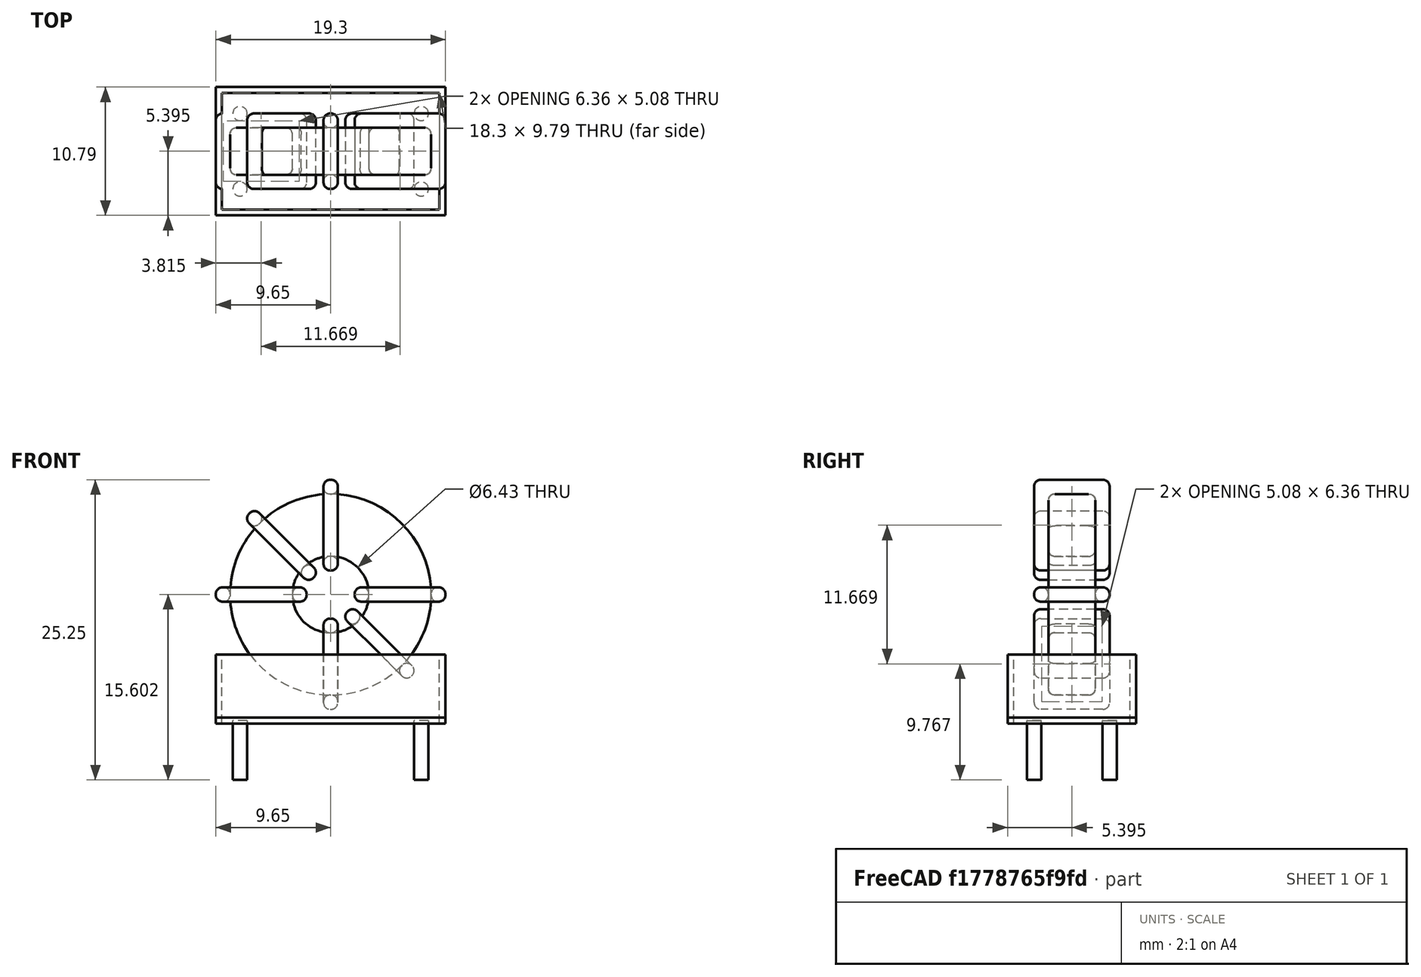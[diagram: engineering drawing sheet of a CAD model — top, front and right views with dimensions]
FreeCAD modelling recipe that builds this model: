
FCSTD DOCUMENT  (FreeCAD 0.16R6703 (Git))
Label: L_CommonModeChoke_Toroid_Vertical_L19.3mm_W10.8mm_Px6.35mm_Py15.24mm_Bourns_8100series
License: All rights reserved
LicenseURL: http://en.wikipedia.org/wiki/All_rights_reserved
objects: Sketcher::SketchObject×8, PartDesign::Pad×8, PartDesign::Fillet×5, Spreadsheet::Sheet×1
note: 29 computed .brp shape members not serialized (recipe doc carries the construction recipe); baked Part::Feature solids carry a one-line shape summary decoded from their .brp

FEATURE [Spreadsheet::Sheet] Spreadsheet  label="dimensions"
  cells = A1=Wx; B1(Wx)=19.304; C1(WW)=6.434666666666666; D1(iWx)=19.304; A2=Wy; B2(Wy)=6.35; D2(iWy)=10.795; A3=RM; B3(RMx)=6.35; C3(RMy)=15.24; A4=d_wire; B4(d_wire)=1.2; A5=H; B5(H)=31; A6=offsetx; B6(offsetx)=2.032
FEATURE [Sketcher::SketchObject] Sketch
  Placement = pos=(7.62,-3.175,0) rot=(1,0,0;1.5708rad)
  expr: Placement.Base.x = Spreadsheet.RMy / 2
  expr: Constraints[4] = Spreadsheet.WW / 2
  expr: Placement.Base.y = -Spreadsheet.RMx / 2
  expr: Constraints[0] = Spreadsheet.Wx / 2 - Spreadsheet.d_wire
  expr: Constraints[2] = Spreadsheet.Wx / 2 + Spreadsheet.d_wire + 0.5
  sketch-geometry (2):
    g0: Circle CenterX=0 CenterY=11.352 CenterZ=0 NormalX=0 NormalY=0 NormalZ=1 Radius=8.452
    g1: Circle CenterX=0 CenterY=11.352 CenterZ=0 NormalX=0 NormalY=0 NormalZ=1 Radius=3.21733
  constraints (5):
    c: Radius(g0) = 8.452
    c: DistanceX(g-1,g0) = 0
    c: DistanceY(g-1,g0) = 11.352
    c: Coincident(g1,g0)
    c: Radius(g1) = 3.21733
FEATURE [PartDesign::Pad] Pad
  Length = 3.95
  Length2 = 100
  Midplane = true
  Placement = pos=(7.62,-3.175,0) rot=(1,0,0;1.5708rad)
  Sketch = -> Sketch
  Type = 0
  expr: Length = Spreadsheet.Wy - 2 * Spreadsheet.d_wire
FEATURE [Sketcher::SketchObject] Sketch001
  Placement = pos=(0,0,0.75) rot=(0,0,1;0rad)
  expr: Constraints[4] = Spreadsheet.RMy
  expr: Constraints[2] = -Spreadsheet.RMx
  expr: Constraints[1] = Spreadsheet.d_wire / 2
  sketch-geometry (4):
    g0: Circle CenterX=0 CenterY=0 CenterZ=0 NormalX=0 NormalY=0 NormalZ=1 Radius=0.6
    g1: Circle CenterX=15.24 CenterY=-6.35 CenterZ=0 NormalX=0 NormalY=0 NormalZ=1 Radius=0.6
    g2: Circle CenterX=0 CenterY=-6.35 CenterZ=0 NormalX=0 NormalY=0 NormalZ=1 Radius=0.6
    g3: Circle CenterX=15.24 CenterY=0 CenterZ=0 NormalX=0 NormalY=0 NormalZ=1 Radius=0.6
  constraints (11):
    c: Equal(g0,g1)
    c: Radius(g0) = 0.6
    c: DistanceY(g-1,g1) = -6.35
    c: Coincident(g0,g-1)
    c: DistanceX(g-1,g1) = 15.24
    c: PointOnObject(g2,g-2)
    c: DistanceY(g-1,g3) = 0
    c: DistanceY(g2,g1) = 0
    c: DistanceX(g3,g1) = 0
    c: Equal(g3,g2)
    c: Equal(g2,g1)
FEATURE [PartDesign::Pad] Pad001
  Length = 5
  Length2 = 0
  Placement = pos=(0,0,0.75) rot=(0,0,1;0rad)
  Reversed = true
  Sketch = -> Sketch001
  Type = 0
FEATURE [PartDesign::Fillet] Fillet
  Base = -> Pad [Edge6,Edge3,Edge2]
  Placement = pos=(7.62,-3.175,0) rot=(1,0,0;1.5708rad)
  Radius = 0.5
FEATURE [Sketcher::SketchObject] Sketch003
  Placement = pos=(7.62,0,11.352) rot=(1,0,0;3.14159rad)
  expr: Placement.Base.x = Spreadsheet.RMy / 2
  expr: Constraints[18] = Spreadsheet.d_wire
  expr: Constraints[16] = Spreadsheet.d_wire
  expr: Constraints[19] = Spreadsheet.d_wire
  expr: Constraints[17] = Spreadsheet.d_wire
  expr: Placement.Base.y = -1 * (Spreadsheet.RMx - Spreadsheet.Wy) / 2
  expr: Constraints[21] = (Spreadsheet.Wx - Spreadsheet.WW) / 2 - Spreadsheet.d_wire
  expr: Constraints[22] = Spreadsheet.Wx / 2 - Spreadsheet.d_wire
  expr: Constraints[43] = Spreadsheet.d_wire
  expr: Constraints[48] = Spreadsheet.Wx - Spreadsheet.d_wire * 2
  expr: Constraints[49] = Spreadsheet.Wy
  expr: Placement.Base.z = Spreadsheet.Wx / 2 + Spreadsheet.d_wire + 0.5
  sketch-geometry (16):
    g0: LineSegment StartX=-2.01733 StartY=0 StartZ=0 EndX=-9.652 EndY=0 EndZ=0
    g1: LineSegment StartX=-9.652 StartY=0 StartZ=0 EndX=-9.652 EndY=6.35 EndZ=0
    g2: LineSegment StartX=-9.652 StartY=6.35 StartZ=0 EndX=-2.01733 EndY=6.35 EndZ=0
    g3: LineSegment StartX=-2.01733 StartY=6.35 StartZ=0 EndX=-2.01733 EndY=0 EndZ=0
    g4: LineSegment StartX=-8.452 StartY=5.15 StartZ=0 EndX=-3.21733 EndY=5.15 EndZ=0
    g5: LineSegment StartX=-3.21733 StartY=5.15 StartZ=0 EndX=-3.21733 EndY=1.2 EndZ=0
    g6: LineSegment StartX=-3.21733 StartY=1.2 StartZ=0 EndX=-8.452 EndY=1.2 EndZ=0
    g7: LineSegment StartX=-8.452 StartY=1.2 StartZ=0 EndX=-8.452 EndY=5.15 EndZ=0
    g8: LineSegment StartX=2.01733 StartY=6.35 StartZ=0 EndX=9.652 EndY=6.35 EndZ=0
    g9: LineSegment StartX=9.652 StartY=6.35 StartZ=0 EndX=9.652 EndY=0 EndZ=0
    g10: LineSegment StartX=9.652 StartY=0 StartZ=0 EndX=2.01733 EndY=0 EndZ=0
    g11: LineSegment StartX=2.01733 StartY=0 StartZ=0 EndX=2.01733 EndY=6.35 EndZ=0
    g12: LineSegment StartX=3.21733 StartY=5.15 StartZ=0 EndX=8.452 EndY=5.15 EndZ=0
    g13: LineSegment StartX=8.452 StartY=5.15 StartZ=0 EndX=8.452 EndY=1.2 EndZ=0
    g14: LineSegment StartX=8.452 StartY=1.2 StartZ=0 EndX=3.21733 EndY=1.2 EndZ=0
    g15: LineSegment StartX=3.21733 StartY=1.2 StartZ=0 EndX=3.21733 EndY=5.15 EndZ=0
  constraints (50):
    c: Horizontal(g0)
    c: Coincident(g1,g0)
    c: Vertical(g1)
    c: Coincident(g2,g1)
    c: Horizontal(g2)
    c: Coincident(g3,g2)
    c: Coincident(g3,g0)
    c: Vertical(g3)
    c: Coincident(g4,g5)
    c: Coincident(g5,g6)
    c: Coincident(g6,g7)
    c: Coincident(g7,g4)
    c: Horizontal(g4)
    c: Horizontal(g6)
    c: Vertical(g5)
    c: Vertical(g7)
    c: DistanceX(g1,g4) = 1.2
    c: DistanceY(g4,g1) = 1.2
    c: DistanceX(g5,g0) = 1.2
    c: DistanceY(g0,g5) = 1.2
    c: DistanceY(g-1,g0) = 0
    c: DistanceX(g6,g6) = 5.23467
    c: DistanceX(g6,g-1) = 8.452
    c: Coincident(g8,g9)
    c: Coincident(g9,g10)
    c: Coincident(g10,g11)
    c: Coincident(g11,g8)
    c: Horizontal(g8)
    c: Horizontal(g10)
    c: Vertical(g9)
    c: Vertical(g11)
    c: Coincident(g12,g13)
    c: Coincident(g13,g14)
    c: Coincident(g14,g15)
    c: Coincident(g15,g12)
    c: Horizontal(g12)
    c: Horizontal(g14)
    c: Vertical(g13)
    c: Vertical(g15)
    c: DistanceY(g8,g2) = 0
    c: DistanceY(g10,g0) = 0
    c: DistanceY(g14,g5) = 0
    c: DistanceY(g12,g4) = 0
    c: DistanceX(g8,g12) = 1.2
    c: Equal(g8,g2)
    c: Equal(g12,g4)
    c: Equal(g9,g1)
    c: Equal(g13,g7)
    c: DistanceX(g4,g12) = 16.904
    c: DistanceY(g0,g1) = 6.35
FEATURE [PartDesign::Pad] Pad002
  Length = 1.2
  Length2 = 100
  Midplane = true
  Placement = pos=(7.62,0,11.352) rot=(1,0,0;3.14159rad)
  Sketch = -> Sketch003
  Type = 0
  expr: Length = Spreadsheet.d_wire
FEATURE [PartDesign::Fillet] Fillet001
  Base = -> Pad002 [Edge38,Edge41,Edge42,Edge43,Edge29,Edge32,Edge33,Edge34,Edge25,Edge35,Edge36,Edge13,Edge14,Edge15,Edge16,Edge17,Edge18,Edge19,Edge1,Edge2,Edge3,Edge4,Edge5,Edge6,Edge7,Edge37,Edge39,Edge40,Edge20,Edge23,Edge24,Edge21,Edge22,Edge8,Edge9,Edge10,Edge11,Edge12,Edge26,Edge27,+8 more]
  Placement = pos=(7.62,0,11.352) rot=(1,0,0;3.14159rad)
  Radius = 0.564
  expr: Radius = Spreadsheet.d_wire * 0.47
FEATURE [Sketcher::SketchObject] Sketch004
  Placement = pos=(7.62,0,11.352) rot=(0.92388,0,0.382683;3.14159rad)
  expr: Placement.Base.x = Spreadsheet.RMy / 2
  expr: Constraints[18] = Spreadsheet.d_wire
  expr: Constraints[16] = Spreadsheet.d_wire
  expr: Constraints[19] = Spreadsheet.d_wire
  expr: Constraints[17] = Spreadsheet.d_wire
  expr: Placement.Base.y = -1 * (Spreadsheet.RMx - Spreadsheet.Wy) / 2
  expr: Constraints[21] = (Spreadsheet.Wx - Spreadsheet.WW) / 2 - Spreadsheet.d_wire
  expr: Constraints[22] = Spreadsheet.Wx / 2 - Spreadsheet.d_wire
  expr: Constraints[43] = Spreadsheet.d_wire
  expr: Constraints[48] = Spreadsheet.Wx - 2 * Spreadsheet.d_wire
  expr: Constraints[49] = Spreadsheet.Wy
  expr: Placement.Base.z = Spreadsheet.Wx / 2 + Spreadsheet.d_wire + 0.5
  sketch-geometry (16):
    g0: LineSegment StartX=-2.01733 StartY=0 StartZ=0 EndX=-9.652 EndY=0 EndZ=0
    g1: LineSegment StartX=-9.652 StartY=0 StartZ=0 EndX=-9.652 EndY=6.35 EndZ=0
    g2: LineSegment StartX=-9.652 StartY=6.35 StartZ=0 EndX=-2.01733 EndY=6.35 EndZ=0
    g3: LineSegment StartX=-2.01733 StartY=6.35 StartZ=0 EndX=-2.01733 EndY=0 EndZ=0
    g4: LineSegment StartX=-8.452 StartY=5.15 StartZ=0 EndX=-3.21733 EndY=5.15 EndZ=0
    g5: LineSegment StartX=-3.21733 StartY=5.15 StartZ=0 EndX=-3.21733 EndY=1.2 EndZ=0
    g6: LineSegment StartX=-3.21733 StartY=1.2 StartZ=0 EndX=-8.452 EndY=1.2 EndZ=0
    g7: LineSegment StartX=-8.452 StartY=1.2 StartZ=0 EndX=-8.452 EndY=5.15 EndZ=0
    g8: LineSegment StartX=2.01733 StartY=6.35 StartZ=0 EndX=9.652 EndY=6.35 EndZ=0
    g9: LineSegment StartX=9.652 StartY=6.35 StartZ=0 EndX=9.652 EndY=0 EndZ=0
    g10: LineSegment StartX=9.652 StartY=0 StartZ=0 EndX=2.01733 EndY=0 EndZ=0
    g11: LineSegment StartX=2.01733 StartY=0 StartZ=0 EndX=2.01733 EndY=6.35 EndZ=0
    g12: LineSegment StartX=3.21733 StartY=5.15 StartZ=0 EndX=8.452 EndY=5.15 EndZ=0
    g13: LineSegment StartX=8.452 StartY=5.15 StartZ=0 EndX=8.452 EndY=1.2 EndZ=0
    g14: LineSegment StartX=8.452 StartY=1.2 StartZ=0 EndX=3.21733 EndY=1.2 EndZ=0
    g15: LineSegment StartX=3.21733 StartY=1.2 StartZ=0 EndX=3.21733 EndY=5.15 EndZ=0
  constraints (50):
    c: Horizontal(g0)
    c: Coincident(g1,g0)
    c: Vertical(g1)
    c: Coincident(g2,g1)
    c: Horizontal(g2)
    c: Coincident(g3,g2)
    c: Coincident(g3,g0)
    c: Vertical(g3)
    c: Coincident(g4,g5)
    c: Coincident(g5,g6)
    c: Coincident(g6,g7)
    c: Coincident(g7,g4)
    c: Horizontal(g4)
    c: Horizontal(g6)
    c: Vertical(g5)
    c: Vertical(g7)
    c: DistanceX(g1,g4) = 1.2
    c: DistanceY(g4,g1) = 1.2
    c: DistanceX(g5,g0) = 1.2
    c: DistanceY(g0,g5) = 1.2
    c: DistanceY(g-1,g0) = 0
    c: DistanceX(g6,g6) = 5.23467
    c: DistanceX(g6,g-1) = 8.452
    c: Coincident(g8,g9)
    c: Coincident(g9,g10)
    c: Coincident(g10,g11)
    c: Coincident(g11,g8)
    c: Horizontal(g8)
    c: Horizontal(g10)
    c: Vertical(g9)
    c: Vertical(g11)
    c: Coincident(g12,g13)
    c: Coincident(g13,g14)
    c: Coincident(g14,g15)
    c: Coincident(g15,g12)
    c: Horizontal(g12)
    c: Horizontal(g14)
    c: Vertical(g13)
    c: Vertical(g15)
    c: DistanceY(g8,g2) = 0
    c: DistanceY(g10,g0) = 0
    c: DistanceY(g14,g5) = 0
    c: DistanceY(g12,g4) = 0
    c: DistanceX(g8,g12) = 1.2
    c: Equal(g8,g2)
    c: Equal(g12,g4)
    c: Equal(g9,g1)
    c: Equal(g13,g7)
    c: DistanceX(g4,g12) = 16.904
    c: DistanceY(g0,g1) = 6.35
FEATURE [PartDesign::Pad] Pad003
  Length = 1.2
  Length2 = 100
  Midplane = true
  Placement = pos=(7.62,0,11.352) rot=(0.92388,0,0.382683;3.14159rad)
  Sketch = -> Sketch004
  Type = 0
  expr: Length = Spreadsheet.d_wire
FEATURE [PartDesign::Fillet] Fillet002
  Base = -> Pad003 [Edge38,Edge41,Edge42,Edge43,Edge29,Edge32,Edge33,Edge34,Edge25,Edge35,Edge36,Edge13,Edge14,Edge15,Edge16,Edge17,Edge18,Edge19,Edge1,Edge2,Edge3,Edge4,Edge5,Edge6,Edge7,Edge37,Edge39,Edge40,Edge20,Edge23,Edge24,Edge21,Edge22,Edge8,Edge9,Edge10,Edge11,Edge12,Edge26,Edge27,+8 more]
  Placement = pos=(7.62,0,11.352) rot=(0.92388,0,0.382683;3.14159rad)
  Radius = 0.564
  expr: Radius = Spreadsheet.d_wire * 0.47
FEATURE [Sketcher::SketchObject] Sketch005
  Placement = pos=(7.62,0,11.352) rot=(0.92388,0,-0.382683;3.14159rad)
  expr: Placement.Base.x = Spreadsheet.RMy / 2
  expr: Constraints[18] = Spreadsheet.d_wire
  expr: Constraints[16] = Spreadsheet.d_wire
  expr: Constraints[19] = Spreadsheet.d_wire
  expr: Constraints[17] = Spreadsheet.d_wire
  expr: Placement.Base.y = -1 * (Spreadsheet.RMx - Spreadsheet.Wy) / 2
  expr: Constraints[21] = (Spreadsheet.Wx - Spreadsheet.WW) / 2 - Spreadsheet.d_wire
  expr: Constraints[22] = Spreadsheet.Wx / 2 - Spreadsheet.d_wire
  expr: Constraints[43] = Spreadsheet.d_wire
  expr: Constraints[48] = Spreadsheet.Wx - 2 * Spreadsheet.d_wire
  expr: Constraints[49] = Spreadsheet.Wy
  expr: Placement.Base.z = Spreadsheet.Wx / 2 + Spreadsheet.d_wire + 0.5
  sketch-geometry (16):
    g0: LineSegment StartX=-2.01733 StartY=0 StartZ=0 EndX=-9.652 EndY=0 EndZ=0
    g1: LineSegment StartX=-9.652 StartY=0 StartZ=0 EndX=-9.652 EndY=6.35 EndZ=0
    g2: LineSegment StartX=-9.652 StartY=6.35 StartZ=0 EndX=-2.01733 EndY=6.35 EndZ=0
    g3: LineSegment StartX=-2.01733 StartY=6.35 StartZ=0 EndX=-2.01733 EndY=0 EndZ=0
    g4: LineSegment StartX=-8.452 StartY=5.15 StartZ=0 EndX=-3.21733 EndY=5.15 EndZ=0
    g5: LineSegment StartX=-3.21733 StartY=5.15 StartZ=0 EndX=-3.21733 EndY=1.2 EndZ=0
    g6: LineSegment StartX=-3.21733 StartY=1.2 StartZ=0 EndX=-8.452 EndY=1.2 EndZ=0
    g7: LineSegment StartX=-8.452 StartY=1.2 StartZ=0 EndX=-8.452 EndY=5.15 EndZ=0
    g8: LineSegment StartX=2.01733 StartY=6.35 StartZ=0 EndX=9.652 EndY=6.35 EndZ=0
    g9: LineSegment StartX=9.652 StartY=6.35 StartZ=0 EndX=9.652 EndY=0 EndZ=0
    g10: LineSegment StartX=9.652 StartY=0 StartZ=0 EndX=2.01733 EndY=0 EndZ=0
    g11: LineSegment StartX=2.01733 StartY=0 StartZ=0 EndX=2.01733 EndY=6.35 EndZ=0
    g12: LineSegment StartX=3.21733 StartY=5.15 StartZ=0 EndX=8.452 EndY=5.15 EndZ=0
    g13: LineSegment StartX=8.452 StartY=5.15 StartZ=0 EndX=8.452 EndY=1.2 EndZ=0
    g14: LineSegment StartX=8.452 StartY=1.2 StartZ=0 EndX=3.21733 EndY=1.2 EndZ=0
    g15: LineSegment StartX=3.21733 StartY=1.2 StartZ=0 EndX=3.21733 EndY=5.15 EndZ=0
  constraints (50):
    c: Horizontal(g0)
    c: Coincident(g1,g0)
    c: Vertical(g1)
    c: Coincident(g2,g1)
    c: Horizontal(g2)
    c: Coincident(g3,g2)
    c: Coincident(g3,g0)
    c: Vertical(g3)
    c: Coincident(g4,g5)
    c: Coincident(g5,g6)
    c: Coincident(g6,g7)
    c: Coincident(g7,g4)
    c: Horizontal(g4)
    c: Horizontal(g6)
    c: Vertical(g5)
    c: Vertical(g7)
    c: DistanceX(g1,g4) = 1.2
    c: DistanceY(g4,g1) = 1.2
    c: DistanceX(g5,g0) = 1.2
    c: DistanceY(g0,g5) = 1.2
    c: DistanceY(g-1,g0) = 0
    c: DistanceX(g6,g6) = 5.23467
    c: DistanceX(g6,g-1) = 8.452
    c: Coincident(g8,g9)
    c: Coincident(g9,g10)
    c: Coincident(g10,g11)
    c: Coincident(g11,g8)
    c: Horizontal(g8)
    c: Horizontal(g10)
    c: Vertical(g9)
    c: Vertical(g11)
    c: Coincident(g12,g13)
    c: Coincident(g13,g14)
    c: Coincident(g14,g15)
    c: Coincident(g15,g12)
    c: Horizontal(g12)
    c: Horizontal(g14)
    c: Vertical(g13)
    c: Vertical(g15)
    c: DistanceY(g8,g2) = 0
    c: DistanceY(g10,g0) = 0
    c: DistanceY(g14,g5) = 0
    c: DistanceY(g12,g4) = 0
    c: DistanceX(g8,g12) = 1.2
    c: Equal(g8,g2)
    c: Equal(g12,g4)
    c: Equal(g9,g1)
    c: Equal(g13,g7)
    c: DistanceX(g4,g12) = 16.904
    c: DistanceY(g0,g1) = 6.35
FEATURE [PartDesign::Pad] Pad004
  Length = 1.2
  Length2 = 100
  Midplane = true
  Placement = pos=(7.62,0,11.352) rot=(0.92388,0,-0.382683;3.14159rad)
  Sketch = -> Sketch005
  Type = 0
  expr: Length = Spreadsheet.d_wire
FEATURE [PartDesign::Fillet] Fillet003
  Base = -> Pad004 [Edge38,Edge41,Edge42,Edge43,Edge29,Edge32,Edge33,Edge34,Edge25,Edge35,Edge36,Edge13,Edge14,Edge15,Edge16,Edge17,Edge18,Edge19,Edge1,Edge2,Edge3,Edge4,Edge5,Edge6,Edge7,Edge37,Edge39,Edge40,Edge20,Edge23,Edge24,Edge21,Edge22,Edge8,Edge9,Edge10,Edge11,Edge12,Edge26,Edge27,+8 more]
  Placement = pos=(7.62,0,11.352) rot=(0.92388,0,-0.382683;3.14159rad)
  Radius = 0.564
  expr: Radius = Spreadsheet.d_wire * 0.47
FEATURE [Sketcher::SketchObject] Sketch006
  Placement = pos=(7.62,0,11.352) rot=(0.707107,0,0.707107;3.14159rad)
  expr: Placement.Base.x = Spreadsheet.RMy / 2
  expr: Constraints[18] = Spreadsheet.d_wire
  expr: Constraints[16] = Spreadsheet.d_wire
  expr: Constraints[19] = Spreadsheet.d_wire
  expr: Constraints[17] = Spreadsheet.d_wire
  expr: Placement.Base.y = -1 * (Spreadsheet.RMx - Spreadsheet.Wy) / 2
  expr: Constraints[21] = (Spreadsheet.Wx - Spreadsheet.WW) / 2 - Spreadsheet.d_wire
  expr: Constraints[22] = Spreadsheet.Wx / 2 - Spreadsheet.d_wire
  expr: Constraints[43] = Spreadsheet.d_wire
  expr: Constraints[48] = Spreadsheet.Wx - Spreadsheet.d_wire * 2
  expr: Constraints[49] = Spreadsheet.Wy
  expr: Placement.Base.z = Spreadsheet.Wx / 2 + Spreadsheet.d_wire + 0.5
  sketch-geometry (16):
    g0: LineSegment StartX=-2.01733 StartY=0 StartZ=0 EndX=-9.652 EndY=0 EndZ=0
    g1: LineSegment StartX=-9.652 StartY=0 StartZ=0 EndX=-9.652 EndY=6.35 EndZ=0
    g2: LineSegment StartX=-9.652 StartY=6.35 StartZ=0 EndX=-2.01733 EndY=6.35 EndZ=0
    g3: LineSegment StartX=-2.01733 StartY=6.35 StartZ=0 EndX=-2.01733 EndY=0 EndZ=0
    g4: LineSegment StartX=-8.452 StartY=5.15 StartZ=0 EndX=-3.21733 EndY=5.15 EndZ=0
    g5: LineSegment StartX=-3.21733 StartY=5.15 StartZ=0 EndX=-3.21733 EndY=1.2 EndZ=0
    g6: LineSegment StartX=-3.21733 StartY=1.2 StartZ=0 EndX=-8.452 EndY=1.2 EndZ=0
    g7: LineSegment StartX=-8.452 StartY=1.2 StartZ=0 EndX=-8.452 EndY=5.15 EndZ=0
    g8: LineSegment StartX=2.01733 StartY=6.35 StartZ=0 EndX=9.652 EndY=6.35 EndZ=0
    g9: LineSegment StartX=9.652 StartY=6.35 StartZ=0 EndX=9.652 EndY=0 EndZ=0
    g10: LineSegment StartX=9.652 StartY=0 StartZ=0 EndX=2.01733 EndY=0 EndZ=0
    g11: LineSegment StartX=2.01733 StartY=0 StartZ=0 EndX=2.01733 EndY=6.35 EndZ=0
    g12: LineSegment StartX=3.21733 StartY=5.15 StartZ=0 EndX=8.452 EndY=5.15 EndZ=0
    g13: LineSegment StartX=8.452 StartY=5.15 StartZ=0 EndX=8.452 EndY=1.2 EndZ=0
    g14: LineSegment StartX=8.452 StartY=1.2 StartZ=0 EndX=3.21733 EndY=1.2 EndZ=0
    g15: LineSegment StartX=3.21733 StartY=1.2 StartZ=0 EndX=3.21733 EndY=5.15 EndZ=0
  constraints (50):
    c: Horizontal(g0)
    c: Coincident(g1,g0)
    c: Vertical(g1)
    c: Coincident(g2,g1)
    c: Horizontal(g2)
    c: Coincident(g3,g2)
    c: Coincident(g3,g0)
    c: Vertical(g3)
    c: Coincident(g4,g5)
    c: Coincident(g5,g6)
    c: Coincident(g6,g7)
    c: Coincident(g7,g4)
    c: Horizontal(g4)
    c: Horizontal(g6)
    c: Vertical(g5)
    c: Vertical(g7)
    c: DistanceX(g1,g4) = 1.2
    c: DistanceY(g4,g1) = 1.2
    c: DistanceX(g5,g0) = 1.2
    c: DistanceY(g0,g5) = 1.2
    c: DistanceY(g-1,g0) = 0
    c: DistanceX(g6,g6) = 5.23467
    c: DistanceX(g6,g-1) = 8.452
    c: Coincident(g8,g9)
    c: Coincident(g9,g10)
    c: Coincident(g10,g11)
    c: Coincident(g11,g8)
    c: Horizontal(g8)
    c: Horizontal(g10)
    c: Vertical(g9)
    c: Vertical(g11)
    c: Coincident(g12,g13)
    c: Coincident(g13,g14)
    c: Coincident(g14,g15)
    c: Coincident(g15,g12)
    c: Horizontal(g12)
    c: Horizontal(g14)
    c: Vertical(g13)
    c: Vertical(g15)
    c: DistanceY(g8,g2) = 0
    c: DistanceY(g10,g0) = 0
    c: DistanceY(g14,g5) = 0
    c: DistanceY(g12,g4) = 0
    c: DistanceX(g8,g12) = 1.2
    c: Equal(g8,g2)
    c: Equal(g12,g4)
    c: Equal(g9,g1)
    c: Equal(g13,g7)
    c: DistanceX(g4,g12) = 16.904
    c: DistanceY(g0,g1) = 6.35
FEATURE [PartDesign::Pad] Pad005
  Length = 1.2
  Length2 = 100
  Midplane = true
  Placement = pos=(7.62,0,11.352) rot=(0.707107,0,0.707107;3.14159rad)
  Sketch = -> Sketch006
  Type = 0
  expr: Length = Spreadsheet.d_wire
FEATURE [PartDesign::Fillet] Fillet004
  Base = -> Pad005 [Edge38,Edge41,Edge42,Edge43,Edge29,Edge32,Edge33,Edge34,Edge25,Edge35,Edge36,Edge13,Edge14,Edge15,Edge16,Edge17,Edge18,Edge19,Edge1,Edge2,Edge3,Edge4,Edge5,Edge6,Edge7,Edge37,Edge39,Edge40,Edge20,Edge23,Edge24,Edge21,Edge22,Edge8,Edge9,Edge10,Edge11,Edge12,Edge26,Edge27,+8 more]
  Placement = pos=(7.62,0,11.352) rot=(0.707107,0,0.707107;3.14159rad)
  Radius = 0.564
  expr: Radius = Spreadsheet.d_wire * 0.47
FEATURE [Sketcher::SketchObject] Sketch007
  Placement = pos=(7.62,0,0.5) rot=(0,0,1;0rad)
  expr: Placement.Base.x = Spreadsheet.RMy / 2
  expr: Placement.Base.z = 0.5
  expr: Constraints[11] = Spreadsheet.iWx / 2
  expr: Constraints[10] = (Spreadsheet.iWy - Spreadsheet.RMx) / 2
  expr: Constraints[9] = Spreadsheet.iWy
  expr: Constraints[8] = Spreadsheet.iWx
  sketch-geometry (4):
    g0: LineSegment StartX=-9.652 StartY=2.2225 StartZ=0 EndX=9.652 EndY=2.2225 EndZ=0
    g1: LineSegment StartX=9.652 StartY=2.2225 StartZ=0 EndX=9.652 EndY=-8.5725 EndZ=0
    g2: LineSegment StartX=9.652 StartY=-8.5725 StartZ=0 EndX=-9.652 EndY=-8.5725 EndZ=0
    g3: LineSegment StartX=-9.652 StartY=-8.5725 StartZ=0 EndX=-9.652 EndY=2.2225 EndZ=0
  constraints (12):
    c: Coincident(g0,g1)
    c: Coincident(g1,g2)
    c: Coincident(g2,g3)
    c: Coincident(g3,g0)
    c: Horizontal(g0)
    c: Horizontal(g2)
    c: Vertical(g1)
    c: Vertical(g3)
    c: DistanceX(g0,g0) = 19.304
    c: DistanceY(g3,g3) = 10.795
    c: DistanceY(g-1,g0) = 2.2225
    c: DistanceX(g0,g-1) = 9.652
FEATURE [PartDesign::Pad] Pad006
  Length = 0.5
  Length2 = 100
  Placement = pos=(7.62,0,0.5) rot=(0,0,1;0rad)
  Sketch = -> Sketch007
  Type = 0
FEATURE [Sketcher::SketchObject] Sketch008
  Placement = pos=(7.62,0,0.5) rot=(0,0,1;0rad)
  expr: Placement.Base.x = Spreadsheet.RMy / 2
  expr: Constraints[8] = Spreadsheet.iWx
  expr: Constraints[9] = Spreadsheet.iWy
  expr: Constraints[10] = (Spreadsheet.iWy - Spreadsheet.RMx) / 2
  expr: Placement.Base.z = 0.5
  expr: Constraints[21] = 0.5
  expr: Constraints[11] = Spreadsheet.iWx / 2
  sketch-geometry (8):
    g0: LineSegment StartX=-9.652 StartY=2.2225 StartZ=0 EndX=9.652 EndY=2.2225 EndZ=0
    g1: LineSegment StartX=9.652 StartY=2.2225 StartZ=0 EndX=9.652 EndY=-8.5725 EndZ=0
    g2: LineSegment StartX=9.652 StartY=-8.5725 StartZ=0 EndX=-9.652 EndY=-8.5725 EndZ=0
    g3: LineSegment StartX=-9.652 StartY=-8.5725 StartZ=0 EndX=-9.652 EndY=2.2225 EndZ=0
    g4: LineSegment StartX=-9.152 StartY=1.7225 StartZ=0 EndX=9.152 EndY=1.7225 EndZ=0
    g5: LineSegment StartX=9.152 StartY=1.7225 StartZ=0 EndX=9.152 EndY=-8.0725 EndZ=0
    g6: LineSegment StartX=9.152 StartY=-8.0725 StartZ=0 EndX=-9.152 EndY=-8.0725 EndZ=0
    g7: LineSegment StartX=-9.152 StartY=-8.0725 StartZ=0 EndX=-9.152 EndY=1.7225 EndZ=0
  constraints (24):
    c: Coincident(g0,g1)
    c: Coincident(g1,g2)
    c: Coincident(g2,g3)
    c: Coincident(g3,g0)
    c: Horizontal(g0)
    c: Horizontal(g2)
    c: Vertical(g1)
    c: Vertical(g3)
    c: DistanceX(g0,g0) = 19.304
    c: DistanceY(g3,g3) = 10.795
    c: DistanceY(g-1,g0) = 2.2225
    c: DistanceX(g0,g-1) = 9.652
    c: Coincident(g4,g5)
    c: Coincident(g5,g6)
    c: Coincident(g6,g7)
    c: Coincident(g7,g4)
    c: Horizontal(g4)
    c: Horizontal(g6)
    c: Vertical(g5)
    c: Vertical(g7)
    c: DistanceX(g5,g1) = 0.5
    c: DistanceY(g1,g5) = 0.5
    c: DistanceX(g0,g4) = 0.5
    c: DistanceY(g4,g0) = 0.5
FEATURE [PartDesign::Pad] Pad007
  Length = 5.7912
  Length2 = 100
  Placement = pos=(7.62,0,0.5) rot=(0,0,1;0rad)
  Sketch = -> Sketch008
  Type = 0
  expr: Length = Spreadsheet.Wx * 0.3
